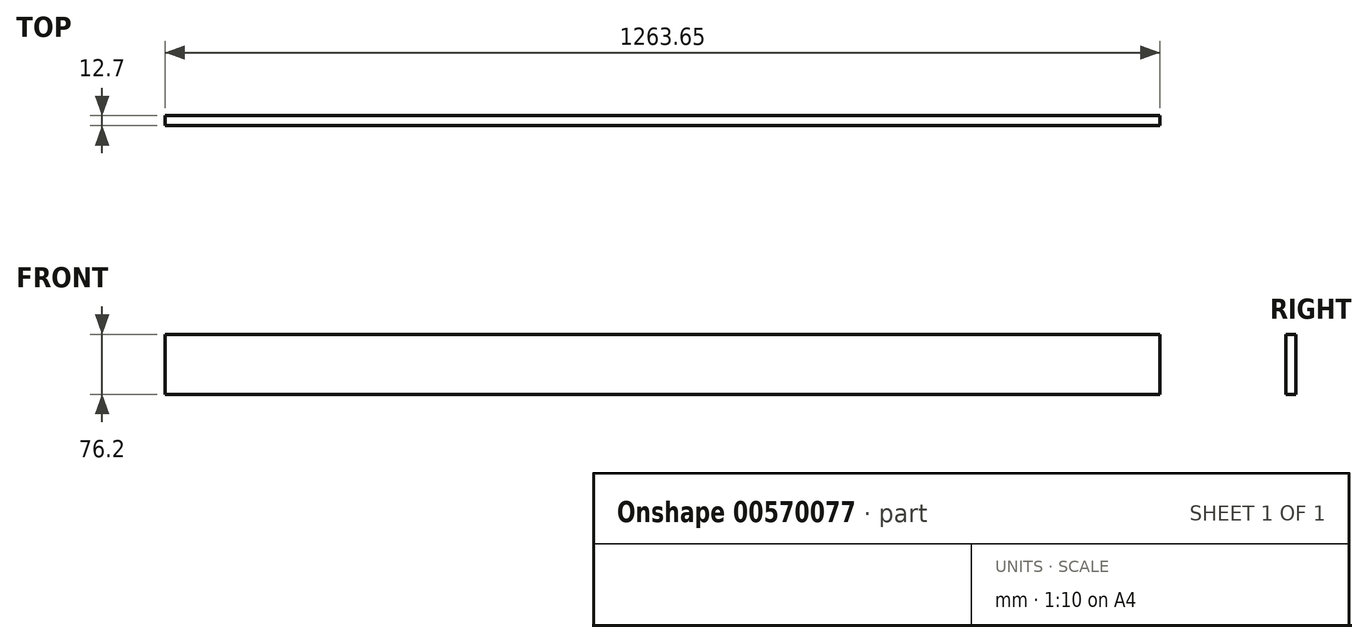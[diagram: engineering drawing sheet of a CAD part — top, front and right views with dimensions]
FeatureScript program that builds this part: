
annotation { "Feature Type Name" : "Feature", "Feature Type Description" : "" }
export const myFeature = defineFeature(function(context is Context, id is Id, definition is map)
    precondition{}
    {
        {
            var Q0;
            Q0=qCreatedBy(makeId("Front.planeOp"),FACE);
            var sketch = newSketch(context, id + "F0", { "sketchPlane" : qUnion([Q0])});
            skLineSegment(sketch, "E0", {"start": v(0, 0) * mm, "end": v(12.7, 0) * mm});
            skLineSegment(sketch, "E1", {"start": v(12.7, 0) * mm, "end": v(12.7, 76.2) * mm});
            skLineSegment(sketch, "E2", {"start": v(12.7, 76.2) * mm, "end": v(0, 76.2) * mm});
            skLineSegment(sketch, "E3", {"start": v(0, 76.2) * mm, "end": v(0, 0) * mm});
            skSolve(sketch);
        }
        {
            var Q0;
            Q0 = qSketchRegion(id + "F0", true);
            extrude(context, id + "F1", {"entities" : qUnion([Q0]), "oppositeDirection" : true, "depth" : 1263.65 * mm, "offsetDistance" : 25.4 * mm});
        }
        {
            var Q0;
            Q0=makeQuery(id+"F1.opExtrude","SWEPT_BODY",BODY,{"disambiguationData":[OSD([sQuery(id+"F0.wireOp",EDGE,"E0"),sQuery(id+"F0.wireOp",EDGE,"E1"),sQuery(id+"F0.wireOp",EDGE,"E2"),sQuery(id+"F0.wireOp",EDGE,"E3")])]});
            var Q1;
            Q1=qCreatedBy(makeId("Origin.pointOp"),VERTEX);
            var Q2;
            Q2=makeQuery(id+"F1.opExtrude","CAP_EDGE",EDGE,{"disambiguationData":[OSD([sQuery(id+"F0.wireOp",EDGE,"E3")])],"isStart":true});
            transform(context, id + "F2", {"entities" : qUnion([Q0]), "transformType" : TransformType.ROTATION, "transformAxis" : qUnion([Q2]), "angle" : 90 * degree, "makeCopy" : false});
        }
    });
